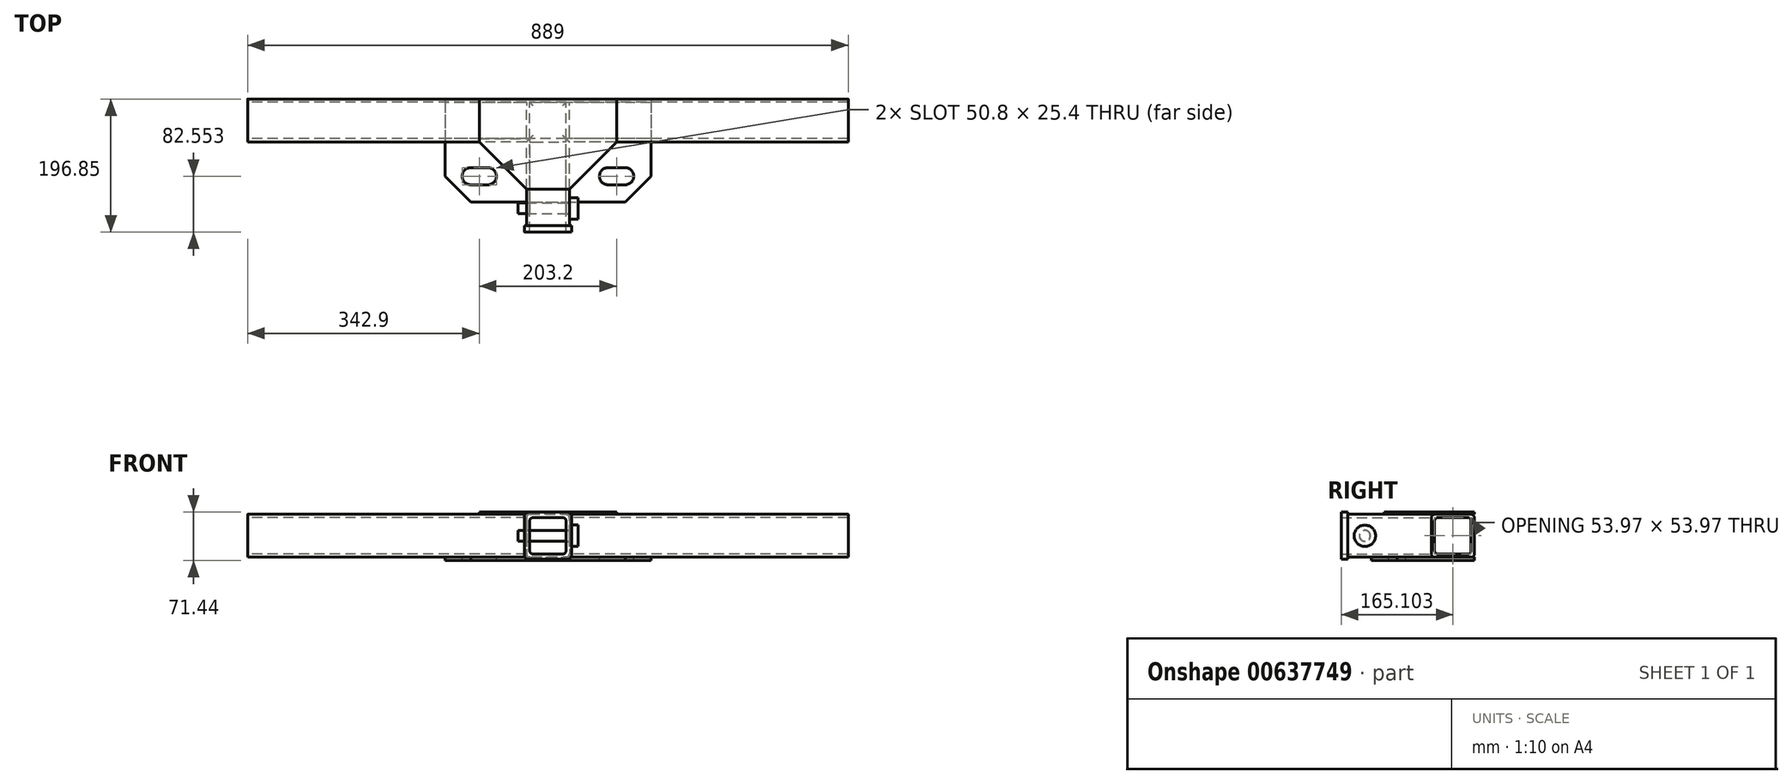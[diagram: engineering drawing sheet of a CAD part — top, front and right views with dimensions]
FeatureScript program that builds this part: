
annotation { "Feature Type Name" : "Feature", "Feature Type Description" : "" }
export const myFeature = defineFeature(function(context is Context, id is Id, definition is map)
    precondition{}
    {
        {
            var Q0;
            Q0=qCreatedBy(makeId("Right.planeOp"),FACE);
            var sketch = newSketch(context, id + "F0", { "sketchPlane" : qUnion([Q0])});
            skLineSegment(sketch, "E0.0", {"start": v(-90.49, 0) * mm, "end": v(-26.99, 0) * mm});
            skLineSegment(sketch, "E0.1", {"start": v(-90.49, 0) * mm, "end": v(-90.49, -63.5) * mm});
            skLineSegment(sketch, "E0.2", {"start": v(-90.49, -63.5) * mm, "end": v(-26.99, -63.5) * mm});
            skLineSegment(sketch, "E0.3", {"start": v(-26.99, 0) * mm, "end": v(-26.99, -63.5) * mm});
            skLineSegment(sketch, "E1.0", {"start": v(-31.75, -4.76) * mm, "end": v(-31.75, -58.74) * mm});
            skLineSegment(sketch, "E1.1", {"start": v(-85.73, -4.76) * mm, "end": v(-31.75, -4.76) * mm});
            skLineSegment(sketch, "E1.2", {"start": v(-85.73, -4.76) * mm, "end": v(-85.73, -58.74) * mm});
            skLineSegment(sketch, "E1.3", {"start": v(-85.73, -58.74) * mm, "end": v(-31.75, -58.74) * mm});
            skSolve(sketch);
        }
        {
            var Q0;
            Q0=makeQuery(id+"F0.imprint","IMPRINT",FACE,{"disambiguationData":[TD([[makeQuery(id+"F0.imprint","IMPRINT",EDGE,{"derivedFrom":sQuery(id+"F0.wireOp",EDGE,"E0.0")}),-1.0]])]});
            var Q1;
            Q1=qConstructionFilter(qBodyType(qCreatedBy(id+"F0",EDGE),BodyType.WIRE),ConstructionObject.NO);
            extrude(context, id + "F1", {"entities" : qUnion([Q0]), "surfaceEntities" : qUnion([Q1]), "endBound" : BoundingType.SYMMETRIC, "depth" : 889 * mm});
        }
        {
            var Q0;
            Q0=makeQuery(id+"F1.opExtrude","SWEPT_FACE",FACE,{"disambiguationData":[OSD([sQuery(id+"F0.wireOp",EDGE,"E0.1")])]});
            var sketch = newSketch(context, id + "F2", { "sketchPlane" : qUnion([Q0])});
            skLineSegment(sketch, "E2.bottom", {"start": v(-31.75, 0) * mm, "end": v(31.75, 0) * mm});
            skLineSegment(sketch, "E2.top", {"start": v(-31.75, -63.5) * mm, "end": v(31.75, -63.5) * mm});
            skLineSegment(sketch, "E2.left", {"start": v(-31.75, 0) * mm, "end": v(-31.75, -63.5) * mm});
            skLineSegment(sketch, "E2.right", {"start": v(31.75, 0) * mm, "end": v(31.75, -63.5) * mm});
            skLineSegment(sketch, "E3.0", {"start": v(-26.99, -4.76) * mm, "end": v(-26.99, -58.74) * mm});
            skLineSegment(sketch, "E3.1", {"start": v(-26.99, -4.76) * mm, "end": v(26.99, -4.76) * mm});
            skLineSegment(sketch, "E3.2", {"start": v(26.99, -4.76) * mm, "end": v(26.99, -58.74) * mm});
            skLineSegment(sketch, "E3.3", {"start": v(-26.99, -58.74) * mm, "end": v(26.99, -58.74) * mm});
            skLineSegment(sketch, "E4", {"start": v(0, 0) * mm, "end": v(0, 11.04) * mm, "construction": true});
            skSolve(sketch);
        }
        {
            var Q0;
            Q0=qSketchRegion(id+"F2",true);
            var Q1;
            Q1=makeQuery(id+"F1.opExtrude","SWEPT_BODY",BODY,{"disambiguationData":[OSD([sQuery(id+"F0.wireOp",EDGE,"E0.0"),sQuery(id+"F0.wireOp",EDGE,"E0.1"),sQuery(id+"F0.wireOp",EDGE,"E0.2"),sQuery(id+"F0.wireOp",EDGE,"E0.3"),sQuery(id+"F0.wireOp",EDGE,"E1.0"),sQuery(id+"F0.wireOp",EDGE,"E1.1"),sQuery(id+"F0.wireOp",EDGE,"E1.2"),sQuery(id+"F0.wireOp",EDGE,"E1.3")])]});
            extrude(context, id + "F3", {"entities" : qUnion([Q0]), "operationType" : NewBodyOperationType.ADD, "depth" : 127 * mm, "hasSecondDirection" : true, "secondDirectionBound" : SecondDirectionBoundingType.UP_TO_BODY, "secondDirectionOppositeDirection" : true, "secondDirectionBoundEntityBody" : qUnion([Q1]), "secondDirectionDepth" : 25.4 * mm});
        }
        {
            var Q0;
            Q0=makeQuery(id+"F1.opExtrude","SWEPT_EDGE",EDGE,{"disambiguationData":[OSD([sQuery(id+"F0.wireOp",EDGE,"E0.0"),sQuery(id+"F0.wireOp",EDGE,"E0.1")])]});
            var Q1;
            Q1=makeQuery(id+"F1.opExtrude","SWEPT_EDGE",EDGE,{"disambiguationData":[OSD([sQuery(id+"F0.wireOp",EDGE,"E0.0"),sQuery(id+"F0.wireOp",EDGE,"E0.3")])]});
            var Q2;
            Q2=makeQuery(id+"F1.opExtrude","SWEPT_EDGE",EDGE,{"disambiguationData":[OSD([sQuery(id+"F0.wireOp",EDGE,"E0.2"),sQuery(id+"F0.wireOp",EDGE,"E0.3")])]});
            var Q3;
            Q3=makeQuery(id+"F1.opExtrude","SWEPT_EDGE",EDGE,{"disambiguationData":[OSD([sQuery(id+"F0.wireOp",EDGE,"E0.1"),sQuery(id+"F0.wireOp",EDGE,"E0.2")])]});
            var Q4;
            Q4=makeQuery(id+"F1.opExtrude","SWEPT_EDGE",EDGE,{"disambiguationData":[OSD([sQuery(id+"F0.wireOp",EDGE,"E1.0"),sQuery(id+"F0.wireOp",EDGE,"E1.1")])]});
            var Q5;
            Q5=makeQuery(id+"F1.opExtrude","SWEPT_EDGE",EDGE,{"disambiguationData":[OSD([sQuery(id+"F0.wireOp",EDGE,"E1.1"),sQuery(id+"F0.wireOp",EDGE,"E1.2")])]});
            var Q6;
            Q6=makeQuery(id+"F1.opExtrude","SWEPT_EDGE",EDGE,{"disambiguationData":[OSD([sQuery(id+"F0.wireOp",EDGE,"E1.0"),sQuery(id+"F0.wireOp",EDGE,"E1.3")])]});
            var Q7;
            Q7=makeQuery(id+"F1.opExtrude","SWEPT_EDGE",EDGE,{"disambiguationData":[OSD([sQuery(id+"F0.wireOp",EDGE,"E1.2"),sQuery(id+"F0.wireOp",EDGE,"E1.3")])]});
            var Q8;
            Q8=makeQuery(id+"F3.opExtrude","SWEPT_EDGE",EDGE,{"disambiguationData":[OSD([sQuery(id+"F0.wireOp",EDGE,"E0.0"),sQuery(id+"F0.wireOp",EDGE,"E0.1"),sQuery(id+"F2.wireOp",EDGE,"E2.bottom"),sQuery(id+"F2.wireOp",EDGE,"E2.left")])]});
            var Q9;
            Q9=makeQuery(id+"F3.opExtrude","SWEPT_EDGE",EDGE,{"disambiguationData":[OSD([sQuery(id+"F0.wireOp",EDGE,"E0.0"),sQuery(id+"F0.wireOp",EDGE,"E0.1"),sQuery(id+"F2.wireOp",EDGE,"E2.bottom"),sQuery(id+"F2.wireOp",EDGE,"E2.right")])]});
            var Q10;
            Q10=makeQuery(id+"F3.opExtrude","SWEPT_EDGE",EDGE,{"disambiguationData":[OSD([sQuery(id+"F0.wireOp",EDGE,"E0.1"),sQuery(id+"F0.wireOp",EDGE,"E0.2"),sQuery(id+"F2.wireOp",EDGE,"E2.top"),sQuery(id+"F2.wireOp",EDGE,"E2.right")])]});
            var Q11;
            Q11=makeQuery(id+"F3.opExtrude","SWEPT_EDGE",EDGE,{"disambiguationData":[OSD([sQuery(id+"F0.wireOp",EDGE,"E0.1"),sQuery(id+"F0.wireOp",EDGE,"E0.2"),sQuery(id+"F2.wireOp",EDGE,"E2.top"),sQuery(id+"F2.wireOp",EDGE,"E2.left")])]});
            var Q12;
            {var subQ0=sQuery(id+"F2.wireOp",EDGE,"E3.1");var subQ1=sQuery(id+"F2.wireOp",EDGE,"E3.0");Q12=makeQuery(id+"F3.boolean.opBoolean","SPLIT",EDGE,{"disambiguationData":[TD([makeQuery(id+"F1.opExtrude","SWEPT_FACE",FACE,{"disambiguationData":[OSD([sQuery(id+"F0.wireOp",EDGE,"E0.1")])]})])],"derivedFrom":makeQuery(id+"F3.opExtrude","SWEPT_EDGE",EDGE,{"disambiguationData":[OSD([subQ1,subQ0])]})});}
            var Q13;
            {var subQ0=sQuery(id+"F2.wireOp",EDGE,"E3.2");var subQ1=sQuery(id+"F2.wireOp",EDGE,"E3.1");Q13=makeQuery(id+"F3.boolean.opBoolean","SPLIT",EDGE,{"disambiguationData":[TD([makeQuery(id+"F1.opExtrude","SWEPT_FACE",FACE,{"disambiguationData":[OSD([sQuery(id+"F0.wireOp",EDGE,"E0.1")])]})])],"derivedFrom":makeQuery(id+"F3.opExtrude","SWEPT_EDGE",EDGE,{"disambiguationData":[OSD([subQ1,subQ0])]})});}
            var Q14;
            {var subQ0=sQuery(id+"F2.wireOp",EDGE,"E3.3");var subQ1=sQuery(id+"F2.wireOp",EDGE,"E3.0");Q14=makeQuery(id+"F3.boolean.opBoolean","SPLIT",EDGE,{"disambiguationData":[TD([makeQuery(id+"F1.opExtrude","SWEPT_FACE",FACE,{"disambiguationData":[OSD([sQuery(id+"F0.wireOp",EDGE,"E0.1")])]})])],"derivedFrom":makeQuery(id+"F3.opExtrude","SWEPT_EDGE",EDGE,{"disambiguationData":[OSD([subQ1,subQ0])]})});}
            var Q15;
            {var subQ0=sQuery(id+"F2.wireOp",EDGE,"E3.3");var subQ1=sQuery(id+"F2.wireOp",EDGE,"E3.2");Q15=makeQuery(id+"F3.boolean.opBoolean","SPLIT",EDGE,{"disambiguationData":[TD([makeQuery(id+"F1.opExtrude","SWEPT_FACE",FACE,{"disambiguationData":[OSD([sQuery(id+"F0.wireOp",EDGE,"E0.1")])]})])],"derivedFrom":makeQuery(id+"F3.opExtrude","SWEPT_EDGE",EDGE,{"disambiguationData":[OSD([subQ1,subQ0])]})});}
            fillet(context, id + "F4", {"entities" : qUnion([Q0, Q1, Q2, Q3, Q4, Q5, Q6, Q7, Q8, Q9, Q10, Q11, Q12, Q13, Q14, Q15]), "radius" : 5.08 * mm, "tangentPropagation" : true, "allowEdgeOverflow" : false});
        }
        {
            var Q0;
            Q0=makeQuery(id+"F3.boolean.opBoolean","MERGE",FACE,{"derivedFrom":[makeQuery(id+"F1.opExtrude","SWEPT_FACE",FACE,{"disambiguationData":[OSD([sQuery(id+"F0.wireOp",EDGE,"E0.0")])]}),makeQuery(id+"F3.opExtrude","SWEPT_FACE",FACE,{"disambiguationData":[OSD([sQuery(id+"F2.wireOp",EDGE,"E2.bottom")])]})]});
            var sketch = newSketch(context, id + "F5", { "sketchPlane" : qUnion([Q0])});
            skLineSegment(sketch, "E5.0", {"start": v(-444.5, -26.99) * mm, "end": v(444.5, -26.99) * mm});
            skLineSegment(sketch, "E6", {"start": v(0, -3.11) * mm, "end": v(0, -26.99) * mm, "construction": true});
            skLineSegment(sketch, "E7.0", {"start": v(-31.75, -90.49) * mm, "end": v(-444.5, -90.49) * mm});
            skLineSegment(sketch, "E8.0", {"start": v(444.5, -90.49) * mm, "end": v(31.75, -90.49) * mm});
            skLineSegment(sketch, "E9", {"start": v(-101.6, -26.99) * mm, "end": v(-101.6, -90.49) * mm});
            skLineSegment(sketch, "E10.0", {"start": v(-31.75, -217.49) * mm, "end": v(-31.75, -90.49) * mm});
            skLineSegment(sketch, "E10.1", {"start": v(31.75, -90.49) * mm, "end": v(31.75, -217.49) * mm});
            skLineSegment(sketch, "E11", {"start": v(-101.6, -90.49) * mm, "end": v(-31.75, -160.34) * mm});
            skLineSegment(sketch, "E12", {"start": v(-31.75, -160.34) * mm, "end": v(31.75, -160.34) * mm});
            skLineSegment(sketch, "E13", {"start": v(31.75, -160.34) * mm, "end": v(101.6, -90.49) * mm});
            skLineSegment(sketch, "E14", {"start": v(101.6, -90.49) * mm, "end": v(101.6, -26.99) * mm});
            skSolve(sketch);
        }
        {
            var Q0;
            Q0=qSketchRegion(id+"F5",true);
            extrude(context, id + "F6", {"entities" : qUnion([Q0]), "operationType" : NewBodyOperationType.ADD, "depth" : 3.17 * mm});
        }
        {
            var Q0;
            Q0=makeQuery(id+"F3.boolean.opBoolean","MERGE",FACE,{"derivedFrom":[makeQuery(id+"F1.opExtrude","SWEPT_FACE",FACE,{"disambiguationData":[OSD([sQuery(id+"F0.wireOp",EDGE,"E0.2")])]}),makeQuery(id+"F3.opExtrude","SWEPT_FACE",FACE,{"disambiguationData":[OSD([sQuery(id+"F2.wireOp",EDGE,"E2.top")])]})]});
            var sketch = newSketch(context, id + "F7", { "sketchPlane" : qUnion([Q0])});
            skLineSegment(sketch, "E15.0", {"start": v(444.5, 26.99) * mm, "end": v(-444.5, 26.99) * mm});
            skLineSegment(sketch, "E16.bottom", {"start": v(-152.4, 26.99) * mm, "end": v(152.4, 26.99) * mm});
            skLineSegment(sketch, "E16.top", {"start": v(-114.3, 179.39) * mm, "end": v(114.3, 179.39) * mm});
            skLineSegment(sketch, "E16.right", {"start": v(152.4, 26.99) * mm, "end": v(152.4, 141.29) * mm});
            skLineSegment(sketch, "E17", {"start": v(0, 0) * mm, "end": v(0, 26.99) * mm, "construction": true});
            skLineSegment(sketch, "E18", {"start": v(-152.4, 141.29) * mm, "end": v(-114.3, 179.39) * mm});
            skLineSegment(sketch, "E19", {"start": v(-114.3, 179.39) * mm, "end": v(-152.4, 141.29) * mm});
            skLineSegment(sketch, "E20", {"start": v(152.4, 141.29) * mm, "end": v(114.3, 179.39) * mm});
            skLineSegment(sketch, "E21", {"start": v(-152.4, 26.99) * mm, "end": v(-152.4, 141.29) * mm});
            skLineSegment(sketch, "E22.bottom", {"start": v(-114.3, 153.99) * mm, "end": v(-88.9, 153.99) * mm});
            skLineSegment(sketch, "E22.top", {"start": v(-114.3, 128.59) * mm, "end": v(-88.9, 128.59) * mm});
            skLineSegment(sketch, "E22.left", {"start": v(-127, 141.29) * mm, "end": v(-127, 141.29) * mm});
            skLineSegment(sketch, "E22.right", {"start": v(-76.2, 141.29) * mm, "end": v(-76.2, 141.29) * mm});
            skPoint(sketch, "E23.visualSharp", {"position": v(-127, 153.99) * mm});
            skArc(sketch, "E23.filletArc", {"start": v(-114.3, 153.99) * mm, "mid": v(-123.28, 150.27) * mm, "end": v(-127, 141.29) * mm});
            skPoint(sketch, "E24.visualSharp", {"position": v(-76.2, 153.99) * mm});
            skArc(sketch, "E24.filletArc", {"start": v(-76.2, 141.29) * mm, "mid": v(-79.92, 150.27) * mm, "end": v(-88.9, 153.99) * mm});
            skPoint(sketch, "E25.visualSharp", {"position": v(-76.2, 128.59) * mm});
            skArc(sketch, "E25.filletArc", {"start": v(-88.9, 128.59) * mm, "mid": v(-79.92, 132.3) * mm, "end": v(-76.2, 141.29) * mm});
            skPoint(sketch, "E26.visualSharp", {"position": v(-127, 128.59) * mm});
            skArc(sketch, "E26.filletArc", {"start": v(-127, 141.29) * mm, "mid": v(-123.28, 132.3) * mm, "end": v(-114.3, 128.59) * mm});
            skArc(sketch, "E27.MirrorCS", {"start": v(88.9, 128.59) * mm, "mid": v(79.92, 132.3) * mm, "end": v(76.2, 141.29) * mm});
            skArc(sketch, "E28.MirrorCS", {"start": v(76.2, 141.29) * mm, "mid": v(79.92, 150.27) * mm, "end": v(88.9, 153.99) * mm});
            skArc(sketch, "E29.MirrorCS", {"start": v(127, 141.29) * mm, "mid": v(123.28, 132.3) * mm, "end": v(114.3, 128.59) * mm});
            skArc(sketch, "E30.MirrorCS", {"start": v(114.3, 153.99) * mm, "mid": v(123.28, 150.27) * mm, "end": v(127, 141.29) * mm});
            skLineSegment(sketch, "E31.MirrorCS", {"start": v(127, 141.29) * mm, "end": v(127, 141.29) * mm});
            skLineSegment(sketch, "E32.MirrorCS", {"start": v(76.2, 141.29) * mm, "end": v(76.2, 141.29) * mm});
            skPoint(sketch, "E33.MirrorP", {"position": v(76.2, 153.99) * mm});
            skPoint(sketch, "E34.MirrorP", {"position": v(76.2, 128.59) * mm});
            skLineSegment(sketch, "E35.MirrorCS", {"start": v(114.3, 153.99) * mm, "end": v(88.9, 153.99) * mm});
            skLineSegment(sketch, "E36.MirrorCS", {"start": v(114.3, 128.59) * mm, "end": v(88.9, 128.59) * mm});
            skPoint(sketch, "E37.MirrorP", {"position": v(127, 128.59) * mm});
            skPoint(sketch, "E38.MirrorP", {"position": v(127, 153.99) * mm});
            skSolve(sketch);
        }
        {
            var Q0;
            Q0=qSketchRegion(id+"F7",true);
            extrude(context, id + "F8", {"entities" : qUnion([Q0]), "operationType" : NewBodyOperationType.ADD, "depth" : 4.76 * mm});
        }
        {
            var Q0;
            Q0=makeQuery(id+"F3.opExtrude","CAP_FACE",FACE,{"disambiguationData":[OSD([sQuery(id+"F2.wireOp",EDGE,"E2.bottom"),sQuery(id+"F2.wireOp",EDGE,"E2.top"),sQuery(id+"F2.wireOp",EDGE,"E2.left"),sQuery(id+"F2.wireOp",EDGE,"E2.right"),sQuery(id+"F2.wireOp",EDGE,"E3.0"),sQuery(id+"F2.wireOp",EDGE,"E3.1"),sQuery(id+"F2.wireOp",EDGE,"E3.2"),sQuery(id+"F2.wireOp",EDGE,"E3.3")])],"isStart":false});
            var sketch = newSketch(context, id + "F9", { "sketchPlane" : qUnion([Q0])});
            skLineSegment(sketch, "E39.0", {"start": v(-21.9, -4.76) * mm, "end": v(21.9, -4.76) * mm});
            skArc(sketch, "E39.1", {"start": v(-26.99, -9.84) * mm, "mid": v(-25.5, -6.25) * mm, "end": v(-21.9, -4.76) * mm});
            skLineSegment(sketch, "E39.2", {"start": v(-26.99, -9.84) * mm, "end": v(-26.99, -53.66) * mm});
            skArc(sketch, "E39.3", {"start": v(-21.9, -58.74) * mm, "mid": v(-25.5, -57.25) * mm, "end": v(-26.99, -53.66) * mm});
            skLineSegment(sketch, "E39.4", {"start": v(-21.9, -58.74) * mm, "end": v(21.9, -58.74) * mm});
            skArc(sketch, "E39.5", {"start": v(26.99, -53.66) * mm, "mid": v(25.5, -57.25) * mm, "end": v(21.9, -58.74) * mm});
            skLineSegment(sketch, "E39.6", {"start": v(26.99, -9.84) * mm, "end": v(26.99, -53.66) * mm});
            skArc(sketch, "E39.7", {"start": v(21.9, -4.76) * mm, "mid": v(25.5, -6.25) * mm, "end": v(26.99, -9.84) * mm});
            skLineSegment(sketch, "E40.bottom", {"start": v(-28.58, 3.18) * mm, "end": v(28.58, 3.18) * mm});
            skLineSegment(sketch, "E40.top", {"start": v(-28.58, -66.68) * mm, "end": v(28.58, -66.68) * mm});
            skLineSegment(sketch, "E40.left", {"start": v(-34.93, -3.17) * mm, "end": v(-34.93, -60.33) * mm});
            skLineSegment(sketch, "E40.right", {"start": v(34.93, -3.17) * mm, "end": v(34.93, -60.33) * mm});
            skPoint(sketch, "E41.visualSharp", {"position": v(-34.93, 3.18) * mm});
            skArc(sketch, "E41.filletArc", {"start": v(-28.58, 3.17) * mm, "mid": v(-33.07, 1.32) * mm, "end": v(-34.93, -3.17) * mm});
            skPoint(sketch, "E42.visualSharp", {"position": v(34.93, 3.18) * mm});
            skArc(sketch, "E42.filletArc", {"start": v(34.93, -3.17) * mm, "mid": v(33.07, 1.32) * mm, "end": v(28.58, 3.17) * mm});
            skPoint(sketch, "E43.visualSharp", {"position": v(34.93, -66.68) * mm});
            skArc(sketch, "E43.filletArc", {"start": v(28.58, -66.68) * mm, "mid": v(33.07, -64.82) * mm, "end": v(34.93, -60.33) * mm});
            skPoint(sketch, "E44.visualSharp", {"position": v(-34.93, -66.68) * mm});
            skArc(sketch, "E44.filletArc", {"start": v(-34.93, -60.33) * mm, "mid": v(-33.07, -64.82) * mm, "end": v(-28.58, -66.68) * mm});
            skSolve(sketch);
        }
        {
            var Q0;
            Q0=qSketchRegion(id+"F9",true);
            extrude(context, id + "F10", {"entities" : qUnion([Q0]), "operationType" : NewBodyOperationType.ADD, "depth" : 6.35 * mm, "hasSecondDirection" : true, "secondDirectionOppositeDirection" : true, "secondDirectionDepth" : 3.17 * mm});
        }
        {
            var Q0;
            Q0=makeQuery(id+"F10.opExtrude","CAP_FACE",FACE,{"disambiguationData":[OSD([sQuery(id+"F9.wireOp",EDGE,"E39.0"),sQuery(id+"F9.wireOp",EDGE,"E39.1"),sQuery(id+"F9.wireOp",EDGE,"E39.2"),sQuery(id+"F9.wireOp",EDGE,"E39.3"),sQuery(id+"F9.wireOp",EDGE,"E39.4"),sQuery(id+"F9.wireOp",EDGE,"E39.5"),sQuery(id+"F9.wireOp",EDGE,"E39.6"),sQuery(id+"F9.wireOp",EDGE,"E39.7"),sQuery(id+"F9.wireOp",EDGE,"E40.bottom"),sQuery(id+"F9.wireOp",EDGE,"E40.top"),sQuery(id+"F9.wireOp",EDGE,"E40.left"),sQuery(id+"F9.wireOp",EDGE,"E40.right"),sQuery(id+"F9.wireOp",EDGE,"E41.filletArc"),sQuery(id+"F9.wireOp",EDGE,"E42.filletArc"),sQuery(id+"F9.wireOp",EDGE,"E43.filletArc"),sQuery(id+"F9.wireOp",EDGE,"E44.filletArc")])],"isStart":false});
            var sketch = newSketch(context, id + "F11", { "sketchPlane" : qUnion([Q0])});
            skLineSegment(sketch, "E45.bottom", {"start": v(-19.05, -6.35) * mm, "end": v(19.05, -6.35) * mm});
            skLineSegment(sketch, "E45.top", {"start": v(-19.05, -57.15) * mm, "end": v(19.05, -57.15) * mm});
            skLineSegment(sketch, "E45.left", {"start": v(-25.4, -12.7) * mm, "end": v(-25.4, -50.8) * mm});
            skLineSegment(sketch, "E45.right", {"start": v(25.4, -12.7) * mm, "end": v(25.4, -50.8) * mm});
            skLineSegment(sketch, "E46", {"start": v(0, 0) * mm, "end": v(0, -4.76) * mm, "construction": true});
            skPoint(sketch, "E47.visualSharp", {"position": v(-25.4, -6.35) * mm});
            skArc(sketch, "E47.filletArc", {"start": v(-19.05, -6.35) * mm, "mid": v(-23.54, -8.2) * mm, "end": v(-25.4, -12.7) * mm});
            skPoint(sketch, "E48.visualSharp", {"position": v(25.4, -6.35) * mm});
            skArc(sketch, "E48.filletArc", {"start": v(25.4, -12.7) * mm, "mid": v(23.54, -8.2) * mm, "end": v(19.05, -6.35) * mm});
            skPoint(sketch, "E49.visualSharp", {"position": v(25.4, -57.15) * mm});
            skArc(sketch, "E49.filletArc", {"start": v(19.05, -57.15) * mm, "mid": v(23.54, -55.3) * mm, "end": v(25.4, -50.8) * mm});
            skPoint(sketch, "E50.visualSharp", {"position": v(-25.4, -57.15) * mm});
            skArc(sketch, "E50.filletArc", {"start": v(-25.4, -50.8) * mm, "mid": v(-23.54, -55.3) * mm, "end": v(-19.05, -57.15) * mm});
            skLineSegment(sketch, "E51.bottom", {"start": v(-14.29, -11.11) * mm, "end": v(14.29, -11.11) * mm});
            skLineSegment(sketch, "E51.top", {"start": v(-14.29, -52.39) * mm, "end": v(14.29, -52.39) * mm});
            skLineSegment(sketch, "E51.left", {"start": v(-20.64, -17.46) * mm, "end": v(-20.64, -46.04) * mm});
            skLineSegment(sketch, "E51.right", {"start": v(20.64, -17.46) * mm, "end": v(20.64, -46.04) * mm});
            skPoint(sketch, "E52.visualSharp", {"position": v(-20.64, -11.11) * mm});
            skArc(sketch, "E52.filletArc", {"start": v(-14.29, -11.11) * mm, "mid": v(-18.78, -12.97) * mm, "end": v(-20.64, -17.46) * mm});
            skPoint(sketch, "E53.visualSharp", {"position": v(20.64, -11.11) * mm});
            skArc(sketch, "E53.filletArc", {"start": v(20.64, -17.46) * mm, "mid": v(18.78, -12.97) * mm, "end": v(14.29, -11.11) * mm});
            skPoint(sketch, "E54.visualSharp", {"position": v(-20.64, -52.39) * mm});
            skArc(sketch, "E54.filletArc", {"start": v(-20.64, -46.04) * mm, "mid": v(-18.78, -50.53) * mm, "end": v(-14.29, -52.39) * mm});
            skPoint(sketch, "E55.visualSharp", {"position": v(20.64, -52.39) * mm});
            skArc(sketch, "E55.filletArc", {"start": v(14.29, -52.39) * mm, "mid": v(18.78, -50.53) * mm, "end": v(20.64, -46.04) * mm});
            skSolve(sketch);
        }
        {
            var Q0;
            {var subQ1=sQuery(id+"F2.wireOp",EDGE,"E2.right");Q0=makeQuery(id+"F3.boolean.opBoolean","SPLIT",FACE,{"disambiguationData":[TD([makeQuery(id+"F1.opExtrude","SWEPT_FACE",FACE,{"disambiguationData":[OSD([sQuery(id+"F0.wireOp",EDGE,"E0.0")])]})])],"derivedFrom":makeQuery(id+"F3.opExtrude","SWEPT_FACE",FACE,{"disambiguationData":[OSD([subQ1])]})});}
            var sketch = newSketch(context, id + "F12", { "sketchPlane" : qUnion([Q0])});
            skCircle(sketch, "E56", {"center": v(-188.91, -31.75) * mm, "radius": 8.33 * mm});
            skPoint(sketch, "E57", {"position": v(-214.31, -31.75) * mm});
            skSolve(sketch);
        }
        {
            var Q0;
            Q0=qSketchRegion(id+"F12",true);
            extrude(context, id + "F13", {"entities" : qUnion([Q0]), "operationType" : NewBodyOperationType.REMOVE, "endBound" : BoundingType.THROUGH_ALL, "oppositeDirection" : true, "depth" : 25.4 * mm});
        }
        {
            var Q0;
            {var subQ1=sQuery(id+"F2.wireOp",EDGE,"E2.right");Q0=makeQuery(id+"F3.boolean.opBoolean","SPLIT",FACE,{"disambiguationData":[TD([makeQuery(id+"F1.opExtrude","SWEPT_FACE",FACE,{"disambiguationData":[OSD([sQuery(id+"F0.wireOp",EDGE,"E0.0")])]})])],"derivedFrom":makeQuery(id+"F3.opExtrude","SWEPT_FACE",FACE,{"disambiguationData":[OSD([subQ1])]})});}
            var sketch = newSketch(context, id + "F14", { "sketchPlane" : qUnion([Q0])});
            skCircle(sketch, "E58", {"center": v(-188.91, -31.75) * mm, "radius": 15.88 * mm});
            skSolve(sketch);
        }
        {
            var Q0;
            Q0=qSketchRegion(id+"F14",true);
            extrude(context, id + "F15", {"entities" : qUnion([Q0]), "depth" : 12.7 * mm});
        }
        {
            var Q0;
            Q0=makeQuery(id+"F15.opExtrude","CAP_FACE",FACE,{"disambiguationData":[OSD([sQuery(id+"F14.wireOp",EDGE,"E58")])],"isStart":true});
            var sketch = newSketch(context, id + "F16", { "sketchPlane" : qUnion([Q0])});
            skCircle(sketch, "E59", {"center": v(188.91, -31.75) * mm, "radius": 7.94 * mm});
            skSolve(sketch);
        }
        {
            var Q0;
            Q0=qSketchRegion(id+"F16",true);
            extrude(context, id + "F17", {"entities" : qUnion([Q0]), "operationType" : NewBodyOperationType.ADD, "depth" : 76.2 * mm});
        }
    });
